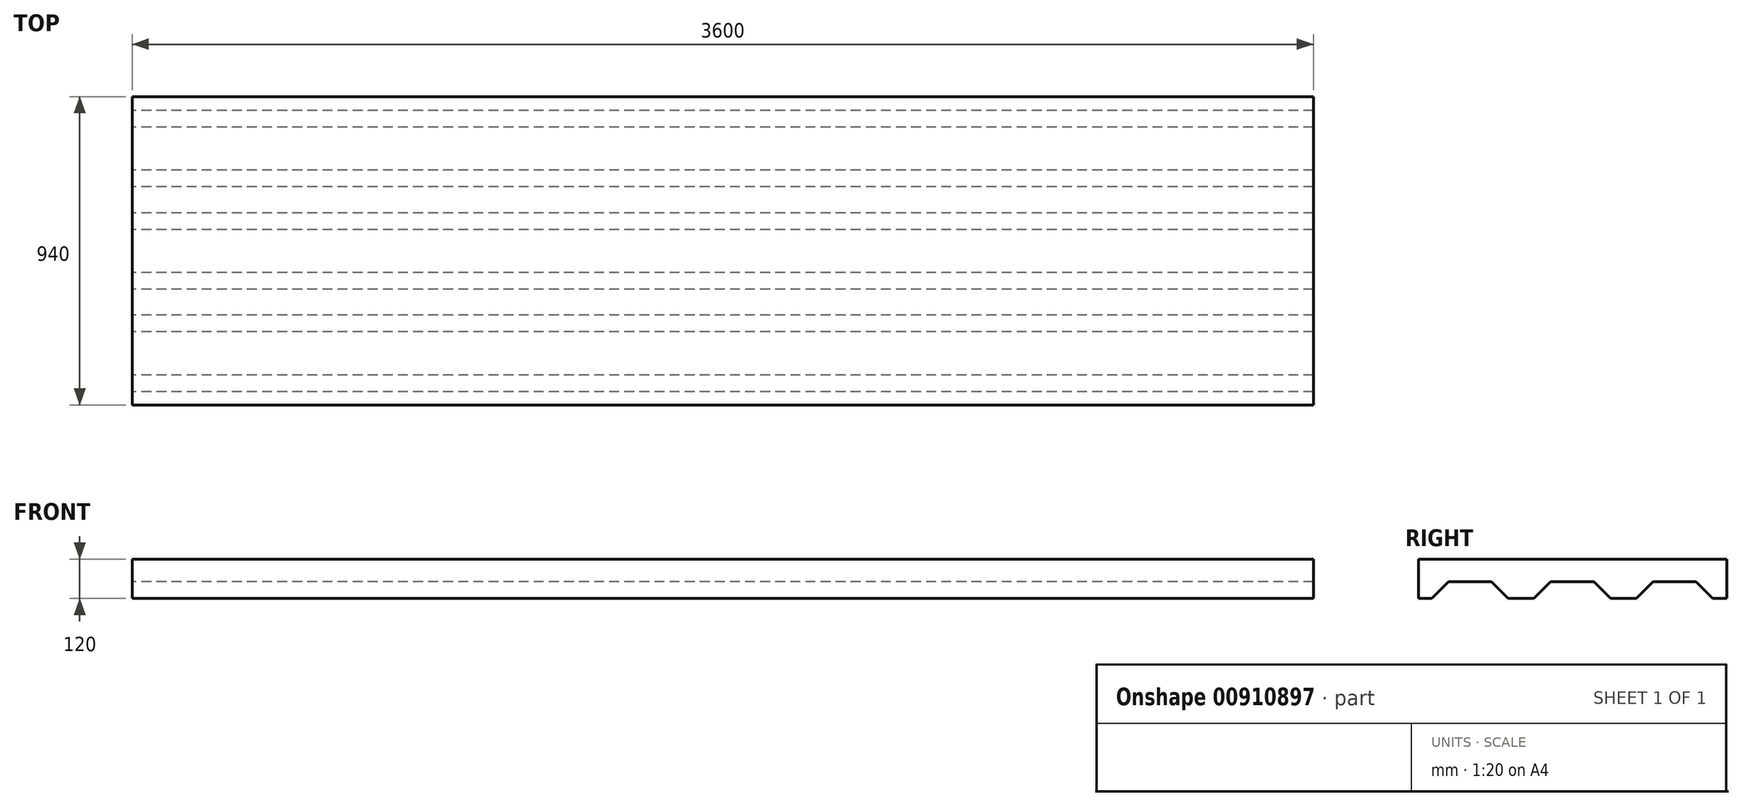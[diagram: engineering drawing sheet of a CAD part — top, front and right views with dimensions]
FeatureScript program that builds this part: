
annotation { "Feature Type Name" : "Feature", "Feature Type Description" : "" }
export const myFeature = defineFeature(function(context is Context, id is Id, definition is map)
    precondition{}
    {
        {
            var Q0;
            Q0=qCreatedBy(makeId("Right.planeOp"),FACE);
            var sketch = newSketch(context, id + "F0", { "sketchPlane" : qUnion([Q0])});
            skLineSegment(sketch, "E0", {"start": v(-213.34, -50.8) * mm, "end": v(-172.76, -50.8) * mm});
            skLineSegment(sketch, "E1", {"start": v(-172.76, -50.8) * mm, "end": v(-121.96, 0) * mm});
            skLineSegment(sketch, "E2", {"start": v(-121.96, 0) * mm, "end": v(9.42, 0) * mm});
            skLineSegment(sketch, "E3", {"start": v(9.42, 0) * mm, "end": v(60.22, -50.8) * mm});
            skLineSegment(sketch, "E4", {"start": v(-56.27, 0) * mm, "end": v(-56.27, -50.8) * mm, "construction": true});
            skLineSegment(sketch, "E5.0", {"start": v(-213.34, 69.2) * mm, "end": v(726.66, 69.2) * mm});
            skLineSegment(sketch, "E6", {"start": v(60.22, -50.8) * mm, "end": v(100.8, -50.8) * mm});
            skLineSegment(sketch, "E7.1.0.0", {"start": v(98.66, -50.8) * mm, "end": v(139.24, -50.8) * mm});
            skLineSegment(sketch, "E7.1.0.1", {"start": v(139.24, -50.8) * mm, "end": v(190.04, 0) * mm});
            skLineSegment(sketch, "E7.1.0.2", {"start": v(190.04, 0) * mm, "end": v(321.42, 0) * mm});
            skLineSegment(sketch, "E7.1.0.3", {"start": v(321.42, 0) * mm, "end": v(372.22, -50.8) * mm});
            skLineSegment(sketch, "E7.1.0.4", {"start": v(372.22, -50.8) * mm, "end": v(412.8, -50.8) * mm});
            skLineSegment(sketch, "E7.2.0.0", {"start": v(410.66, -50.8) * mm, "end": v(451.24, -50.8) * mm});
            skLineSegment(sketch, "E7.2.0.1", {"start": v(451.24, -50.8) * mm, "end": v(502.04, 0) * mm});
            skLineSegment(sketch, "E7.2.0.2", {"start": v(502.04, 0) * mm, "end": v(633.42, 0) * mm});
            skLineSegment(sketch, "E7.2.0.3", {"start": v(633.42, 0) * mm, "end": v(684.22, -50.8) * mm});
            skLineSegment(sketch, "E7.2.0.4", {"start": v(684.22, -50.8) * mm, "end": v(724.8, -50.8) * mm});
            skLineSegment(sketch, "E7.direction1", {"start": v(-213.34, -50.8) * mm, "end": v(98.66, -50.8) * mm, "construction": true});
            skLineSegment(sketch, "E8", {"start": v(-213.34, 69.2) * mm, "end": v(-213.34, -50.8) * mm});
            skLineSegment(sketch, "E9", {"start": v(726.66, 69.2) * mm, "end": v(726.66, -50.8) * mm});
            skLineSegment(sketch, "E10", {"start": v(724.8, -50.8) * mm, "end": v(726.66, -50.8) * mm});
            skSolve(sketch);
        }
        {
            var Q0;
            Q0=makeQuery(id+"F0.imprint","IMPRINT",FACE,{"disambiguationData":[TD([[makeQuery(id+"F0.imprint","IMPRINT",EDGE,{"derivedFrom":sQuery(id+"F0.wireOp",EDGE,"E0")}),1.0]])]});
            extrude(context, id + "F1", {"entities" : qUnion([Q0]), "depth" : 3600 * mm, "offsetDistance" : 25 * mm});
        }
    });
